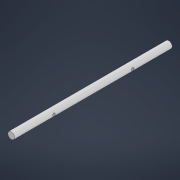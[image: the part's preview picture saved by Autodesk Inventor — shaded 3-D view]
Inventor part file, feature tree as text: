
AUTODESK INVENTOR PART (.ipt)
format: ipt  version: 2022 (Build 260153000, 153)  size: 110,592 bytes
history: native  units: in
note: dims shown in document units (in); Inventor stores cm internally (conversion verified against a paired STEP export)
features: extrude x1, fillet x1, sketch x1
ambient origin geometry x8: Origin, YZ Plane, XZ Plane, XY Plane, X Axis, Y Axis, Z Axis, Center Point
bodies: Solid1 (feature_tree)
feature tree (3):
  extrude  "Extrusion1"  Depth=5.9055in
  fillet  "Fillet1"  Radius=0.3937in
  sketch  "Sketch1"  dims[d0=1.0in d1=23.622in d3=0.3937in d4=1.0in d5=0.0in d6=0.5in d8=5.9055in]
